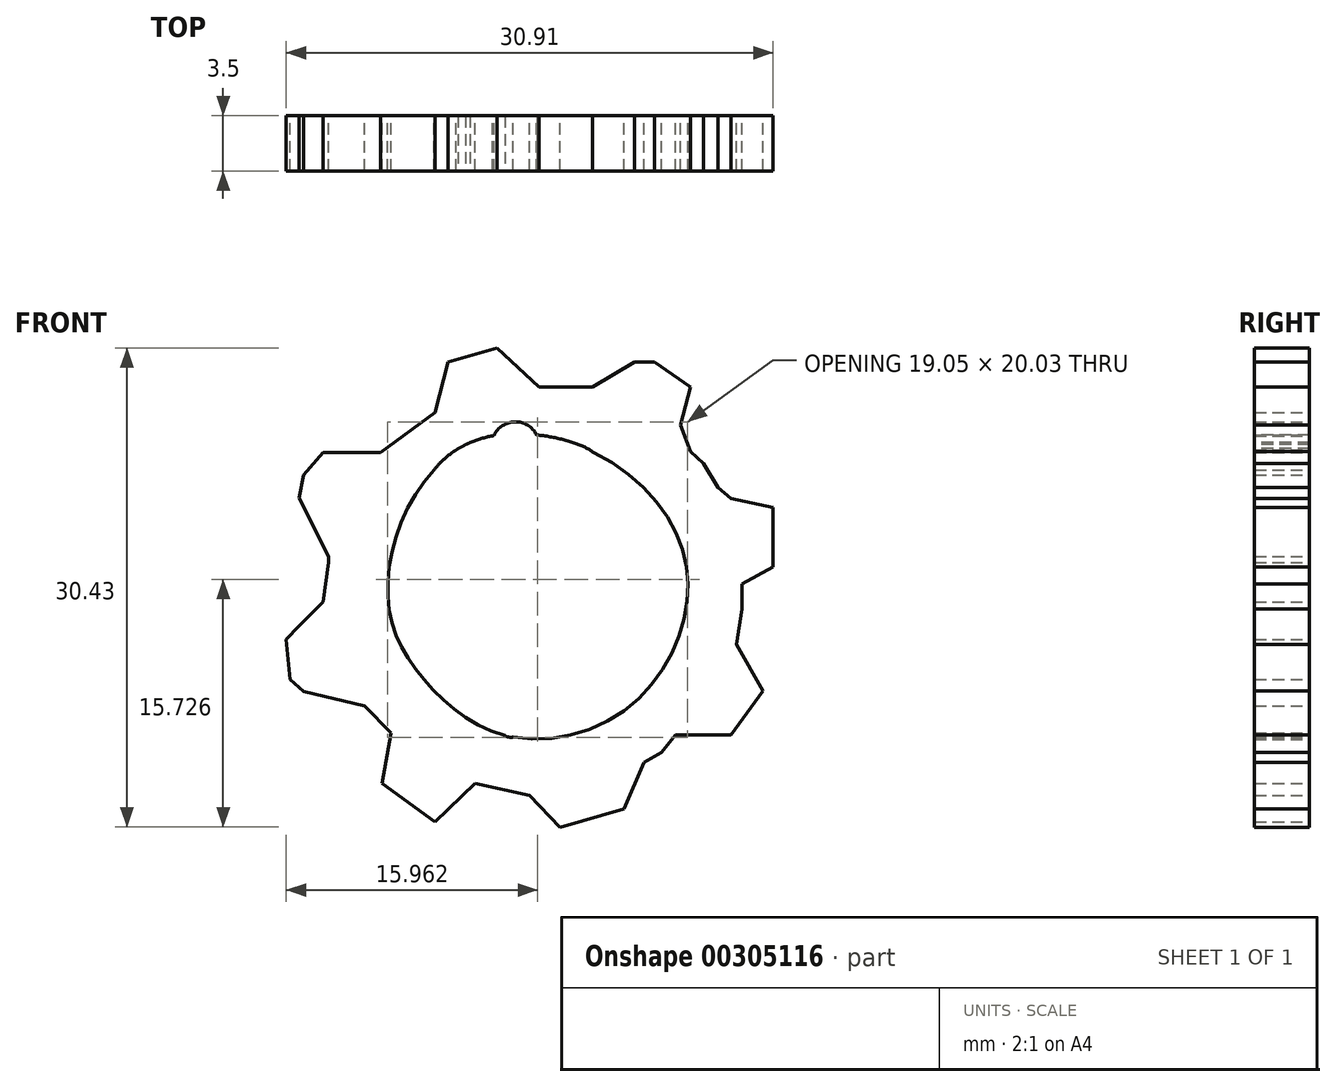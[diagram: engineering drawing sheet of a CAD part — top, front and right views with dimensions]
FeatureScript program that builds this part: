
annotation { "Feature Type Name" : "Feature", "Feature Type Description" : "" }
export const myFeature = defineFeature(function(context is Context, id is Id, definition is map)
    precondition{}
    {
        {
            var Q0;
            Q0=qCreatedBy(makeId("Front.planeOp"),FACE);
            var sketch = newSketch(context, id + "F0", { "sketchPlane" : qUnion([Q0])});
            skLineSegment(sketch, "E0", {"start": v(-29.85, 3.7) * mm, "end": v(-31.8, 5.73) * mm});
            skLineSegment(sketch, "E1", {"start": v(-31.8, 5.73) * mm, "end": v(-35.26, 6.5) * mm});
            skLineSegment(sketch, "E2", {"start": v(-35.26, 6.5) * mm, "end": v(-37.8, 4.04) * mm});
            skLineSegment(sketch, "E3", {"start": v(-37.8, 4.04) * mm, "end": v(-41.17, 6.5) * mm});
            skLineSegment(sketch, "E4", {"start": v(-41.17, 6.5) * mm, "end": v(-40.58, 9.7) * mm});
            skLineSegment(sketch, "E5", {"start": v(-40.58, 9.7) * mm, "end": v(-42.27, 11.4) * mm});
            skLineSegment(sketch, "E6", {"start": v(-42.27, 11.4) * mm, "end": v(-46.15, 12.32) * mm});
            skLineSegment(sketch, "E7", {"start": v(-46.15, 12.32) * mm, "end": v(-47, 13.08) * mm});
            skLineSegment(sketch, "E8", {"start": v(-47, 13.08) * mm, "end": v(-47.25, 15.63) * mm});
            skLineSegment(sketch, "E9", {"start": v(-47.25, 15.63) * mm, "end": v(-46.43, 16.48) * mm});
            skLineSegment(sketch, "E10", {"start": v(-46.43, 16.48) * mm, "end": v(-44.91, 18.03) * mm});
            skLineSegment(sketch, "E11", {"start": v(-44.91, 18.03) * mm, "end": v(-44.55, 20.5) * mm});
            skLineSegment(sketch, "E12", {"start": v(-44.55, 20.5) * mm, "end": v(-44.55, 20.9) * mm});
            skLineSegment(sketch, "E13", {"start": v(-44.55, 20.9) * mm, "end": v(-46.43, 24.6) * mm});
            skLineSegment(sketch, "E14", {"start": v(-46.43, 24.6) * mm, "end": v(-46.15, 26.07) * mm});
            skLineSegment(sketch, "E15", {"start": v(-46.15, 26.07) * mm, "end": v(-44.91, 27.5) * mm});
            skLineSegment(sketch, "E16", {"start": v(-44.91, 27.5) * mm, "end": v(-41.27, 27.5) * mm});
            skLineSegment(sketch, "E17", {"start": v(-41.27, 27.5) * mm, "end": v(-37.8, 30.03) * mm});
            skLineSegment(sketch, "E18", {"start": v(-37.8, 30.03) * mm, "end": v(-36.96, 33.26) * mm});
            skLineSegment(sketch, "E19", {"start": v(-36.96, 33.26) * mm, "end": v(-33.86, 34.14) * mm});
            skLineSegment(sketch, "E20", {"start": v(-33.86, 34.14) * mm, "end": v(-31.2, 31.68) * mm});
            skLineSegment(sketch, "E21", {"start": v(-31.2, 31.68) * mm, "end": v(-29.56, 31.68) * mm});
            skLineSegment(sketch, "E22", {"start": v(-29.56, 31.68) * mm, "end": v(-28.49, 31.68) * mm});
            skLineSegment(sketch, "E23", {"start": v(-28.49, 31.68) * mm, "end": v(-27.79, 31.68) * mm});
            skLineSegment(sketch, "E24", {"start": v(-27.79, 31.68) * mm, "end": v(-25.13, 33.26) * mm});
            skLineSegment(sketch, "E25", {"start": v(-25.13, 33.26) * mm, "end": v(-23.87, 33.26) * mm});
            skLineSegment(sketch, "E26", {"start": v(-23.87, 33.26) * mm, "end": v(-21.59, 31.68) * mm});
            skLineSegment(sketch, "E27", {"start": v(-21.59, 31.68) * mm, "end": v(-22.21, 29.25) * mm});
            skLineSegment(sketch, "E28", {"start": v(-22.21, 29.25) * mm, "end": v(-21.59, 27.56) * mm});
            skLineSegment(sketch, "E29", {"start": v(-21.59, 27.56) * mm, "end": v(-20.77, 26.8) * mm});
            skLineSegment(sketch, "E30", {"start": v(-20.77, 26.8) * mm, "end": v(-19.82, 25.29) * mm});
            skLineSegment(sketch, "E31", {"start": v(-19.82, 25.29) * mm, "end": v(-19, 24.59) * mm});
            skLineSegment(sketch, "E32", {"start": v(-19, 24.59) * mm, "end": v(-16.34, 24.02) * mm});
            skLineSegment(sketch, "E33", {"start": v(-16.34, 24.02) * mm, "end": v(-16.34, 20.22) * mm});
            skLineSegment(sketch, "E34", {"start": v(-16.34, 20.22) * mm, "end": v(-18.3, 19.15) * mm});
            skLineSegment(sketch, "E35", {"start": v(-18.3, 19.15) * mm, "end": v(-18.3, 17.57) * mm});
            skLineSegment(sketch, "E36", {"start": v(-18.3, 17.57) * mm, "end": v(-18.66, 15.32) * mm});
            skLineSegment(sketch, "E37", {"start": v(-18.66, 15.32) * mm, "end": v(-16.96, 12.37) * mm});
            skLineSegment(sketch, "E38", {"start": v(-16.96, 12.37) * mm, "end": v(-19, 9.56) * mm});
            skLineSegment(sketch, "E39", {"start": v(-19, 9.56) * mm, "end": v(-21.57, 9.56) * mm});
            skLineSegment(sketch, "E40", {"start": v(-21.57, 9.56) * mm, "end": v(-22.53, 9.56) * mm});
            skLineSegment(sketch, "E41", {"start": v(-22.53, 9.56) * mm, "end": v(-23.4, 8.44) * mm});
            skLineSegment(sketch, "E42", {"start": v(-23.4, 8.44) * mm, "end": v(-24.52, 7.8) * mm});
            skLineSegment(sketch, "E43", {"start": v(-24.52, 7.8) * mm, "end": v(-25.8, 4.85) * mm});
            skLineSegment(sketch, "E44", {"start": v(-25.8, 4.85) * mm, "end": v(-29.85, 3.7) * mm});
            skFitSpline(sketch, "E45", {"points": [v(-33.6, 20.27) * mm, v(-35.44, 20.7) * mm, v(-36.15, 19.61) * mm, v(-36.15, 19.08) * mm, v(-36.1, 18.52) * mm, v(-35.4, 18.19) * mm, v(-33.92, 18.62) * mm, v(-33.6, 20.27) * mm]});
            skFitSpline(sketch, "E46", {"points": [v(-30.94, 21.03) * mm, v(-28.94, 22.03) * mm, v(-27.9, 21.18) * mm, v(-28.14, 19.8) * mm, v(-30.8, 19.85) * mm, v(-30.95, 20.48) * mm, v(-30.94, 21.03) * mm]});
            skPoint(sketch, "E47.5.internal.snap0", {"position": v(-45.53, 26.79) * mm});
            skPoint(sketch, "E47.5.internal.snap1", {"position": v(-26.46, 32.47) * mm});
            skPoint(sketch, "E47.8.internal.snap0", {"position": v(-26.46, 32.47) * mm});
            skFitSpline(sketch, "E48", {"points": [v(-32.06, 16.68) * mm, v(-32.56, 17.1) * mm, v(-32.68, 18.19) * mm, v(-32.47, 19.08) * mm, v(-32.08, 18.52) * mm, v(-31.66, 17.17) * mm, v(-32.06, 16.68) * mm]});
            skFitSpline(sketch, "E49", {"points": [v(-31.48, 19.08) * mm, v(-31.57, 18.19) * mm, v(-31.21, 16.99) * mm, v(-30.47, 17.26) * mm, v(-30.94, 18.52) * mm, v(-31.48, 19.08) * mm]});
            skFitSpline(sketch, "E50", {"points": [v(-33.6, 12.98) * mm, v(-34.15, 13.04) * mm, v(-34.97, 14.36) * mm, v(-35.4, 15.22) * mm, v(-35, 15.22) * mm, v(-34.74, 14.9) * mm, v(-34.44, 14.94) * mm, v(-34.5, 14.48) * mm, v(-34.15, 13.82) * mm, v(-33.6, 13.52) * mm, v(-33.6, 12.98) * mm]});
            skFitSpline(sketch, "E51", {"points": [v(-32.91, 14.42) * mm, v(-32.56, 12.95) * mm, v(-32.69, 14.25) * mm, v(-32.87, 14.63) * mm, v(-32.91, 14.42) * mm]});
            skFitSpline(sketch, "E52", {"points": [v(-32.73, 12.91) * mm, v(-32.92, 13.58) * mm, v(-33.09, 13.63) * mm, v(-33.11, 13.75) * mm, v(-32.92, 13.72) * mm, v(-32.85, 13.55) * mm, v(-32.66, 12.96) * mm, v(-32.73, 12.91) * mm]});
            skFitSpline(sketch, "E53", {"points": [v(-32.22, 14.54) * mm, v(-32.15, 14.4) * mm, v(-32, 14.68) * mm, v(-32.03, 15.38) * mm, v(-31.84, 15.42) * mm, v(-31.6, 14.23) * mm, v(-31.43, 14.28) * mm, v(-31.43, 15.1) * mm, v(-30.95, 15.33) * mm, v(-30.79, 15.2) * mm, v(-30.83, 15.06) * mm, v(-30.7, 14.68) * mm, v(-30.6, 13.82) * mm, v(-30.25, 12.96) * mm, v(-30.4, 12.66) * mm, v(-30.9, 12.76) * mm, v(-31.13, 13.4) * mm, v(-31.35, 14.2) * mm, v(-31.38, 14.08) * mm, v(-31.6, 14.15) * mm, v(-31.9, 14.17) * mm, v(-31.88, 13.9) * mm, v(-32.2, 14.25) * mm, v(-32.22, 14.54) * mm]});
            skFitSpline(sketch, "E54", {"points": [v(-30.33, 15.06) * mm, v(-30.62, 15.32) * mm, v(-30.35, 15.5) * mm, v(-30.07, 15.42) * mm, v(-29.73, 15.47) * mm, v(-29.5, 15.47) * mm, v(-29.4, 14.76) * mm, v(-29.3, 14.4) * mm, v(-29.24, 14.4) * mm, v(-29.27, 15.4) * mm, v(-29.14, 15.5) * mm, v(-28.98, 15.2) * mm, v(-28.93, 15.06) * mm, v(-29.12, 14.94) * mm, v(-29.05, 14.54) * mm, v(-28.9, 14.56) * mm, v(-28.93, 14.4) * mm, v(-29.12, 14.4) * mm, v(-29.15, 14.28) * mm, v(-29.24, 14.28) * mm, v(-29.25, 14.34) * mm, v(-29.34, 14.35) * mm, v(-29.32, 13.85) * mm, v(-29.4, 13.84) * mm, v(-29.38, 13.55) * mm, v(-29.7, 13.54) * mm, v(-29.74, 13.84) * mm, v(-29.9, 14.06) * mm, v(-30, 14.28) * mm, v(-29.9, 14.4) * mm, v(-30.09, 14.54) * mm, v(-30.23, 14.94) * mm, v(-30.33, 15.06) * mm]});
            skFitSpline(sketch, "E55", {"points": [v(-30.43, 14.7) * mm, v(-30.36, 14.7) * mm, v(-30.32, 14.66) * mm, v(-30.24, 14.3) * mm, v(-29.83, 13.42) * mm, v(-29.89, 13.14) * mm, v(-30.1, 13.15) * mm, v(-30.13, 13.46) * mm, v(-30.29, 13.67) * mm, v(-30.32, 14.02) * mm, v(-30.3, 14.14) * mm, v(-30.42, 14.21) * mm, v(-30.5, 14.6) * mm, v(-30.43, 14.7) * mm]});
            skFitSpline(sketch, "E56", {"points": [v(-29.12, 13.55) * mm, v(-29.12, 14.06) * mm, v(-28.96, 14.02) * mm, v(-28.9, 13.6) * mm, v(-29.12, 13.55) * mm]});
            skFitSpline(sketch, "E57", {"points": [v(-28.76, 14.02) * mm, v(-28.82, 14.06) * mm, v(-28.79, 13.85) * mm, v(-28.73, 13.87) * mm, v(-28.76, 14.02) * mm]});
            skFitSpline(sketch, "E58", {"points": [v(-28.68, 15.5) * mm, v(-28.8, 15.5) * mm, v(-28.82, 15.18) * mm, v(-28.8, 14.94) * mm, v(-28.7, 14.54) * mm, v(-28.7, 14.4) * mm, v(-28.6, 14.52) * mm, v(-28.56, 14.74) * mm, v(-28.6, 14.94) * mm, v(-28.63, 15.06) * mm, v(-28.65, 15.1) * mm, v(-28.65, 15.3) * mm, v(-28.68, 15.5) * mm]});
            skFitSpline(sketch, "E59", {"points": [v(-28.19, 15.02) * mm, v(-28.32, 15.06) * mm, v(-28.3, 14.68) * mm, v(-28.17, 14.68) * mm, v(-28.08, 14.54) * mm, v(-27.98, 14.54) * mm, v(-28.03, 14.76) * mm, v(-28.12, 14.78) * mm, v(-28.17, 14.94) * mm, v(-28.19, 15.02) * mm]});
            skFitSpline(sketch, "E60", {"points": [v(-27.73, 14.28) * mm, v(-27.8, 14.48) * mm, v(-27.64, 14.46) * mm, v(-27.58, 14.28) * mm, v(-27.73, 14.28) * mm]});
            skFitSpline(sketch, "E61", {"points": [v(-27.48, 14.5) * mm, v(-27.25, 15.81) * mm, v(-27.32, 16.34) * mm, v(-27.36, 16.91) * mm, v(-28.05, 16.53) * mm, v(-28.06, 16) * mm, v(-27.87, 16.14) * mm, v(-27.68, 16.02) * mm, v(-27.57, 16.2) * mm, v(-27.37, 16.1) * mm, v(-27.42, 15.8) * mm, v(-27.54, 15.07) * mm, v(-27.75, 15.23) * mm, v(-27.9, 15.2) * mm, v(-27.73, 14.85) * mm, v(-27.48, 14.5) * mm]});
            skFitSpline(sketch, "E62", {"points": [v(-26.75, 16.52) * mm, v(-27, 16.53) * mm, v(-26.94, 16.16) * mm, v(-26.9, 15.94) * mm, v(-27.05, 15.8) * mm, v(-27.12, 15.52) * mm, v(-27.17, 15.37) * mm, v(-27.24, 15.1) * mm, v(-27.17, 14.76) * mm, v(-27.06, 14.55) * mm, v(-27, 14.84) * mm, v(-26.9, 15.26) * mm, v(-26.84, 15.53) * mm, v(-26.82, 15.8) * mm, v(-26.75, 16.16) * mm, v(-26.83, 16.29) * mm, v(-26.75, 16.52) * mm]});
            skPoint(sketch, "E63.2.internal.snap0", {"position": v(-35.41, 33.7) * mm});
            skFitSpline(sketch, "E64.trimOffspring", {"points": [v(-33.37, 9.53) * mm, v(-38.43, 13) * mm, v(-40.74, 17.7) * mm, v(-39.3, 24.42) * mm, v(-34.15, 28.56) * mm, v(-26.46, 26.79) * mm, v(-22.16, 21.55) * mm, v(-22.32, 15.8) * mm, v(-26.46, 10.66) * mm, v(-33.37, 9.53) * mm]});
            skFitSpline(sketch, "E65.trimOffspring", {"points": [v(-37.87, 26.38) * mm, v(-36.47, 27.66) * mm, v(-36.33, 27.74) * mm, v(-35.85, 28) * mm, v(-35.56, 28.13) * mm, v(-34.15, 28.56) * mm, v(-31.33, 28.62) * mm, v(-27.75, 27.5) * mm, v(-26.97, 26.52) * mm, v(-26.46, 26.07) * mm, v(-26.46, 23.07) * mm, v(-27.14, 21.9) * mm, v(-27.14, 19.95) * mm, v(-25.83, 18.95) * mm, v(-26, 17.92) * mm, v(-26.46, 17.4) * mm, v(-26.75, 14.55) * mm, v(-27.13, 11.93) * mm, v(-29.16, 10.63) * mm, v(-33.37, 9.53) * mm, v(-33.37, 10.53) * mm, v(-34.3, 11.06) * mm, v(-35.4, 13.27) * mm, v(-36.87, 14.35) * mm], "startDerivative": vector(38.58, 35.58) * mm, "endDerivative": vector(-36.08, 16.17) * mm});
            skFitSpline(sketch, "E66.trimOffspring", {"points": [v(-33.37, 9.53) * mm, v(-33.37, 10.53) * mm, v(-34.3, 11.06) * mm, v(-35.4, 13.27) * mm, v(-36.87, 14.35) * mm, v(-38.72, 17.45) * mm, v(-38.54, 19.61) * mm, v(-39.55, 21.34) * mm, v(-38.6, 24.74) * mm, v(-37.87, 26.38) * mm, v(-34.15, 28.56) * mm, v(-27.75, 27.5) * mm, v(-26.97, 26.52) * mm, v(-26.46, 26.07) * mm, v(-26.46, 23.07) * mm, v(-27.14, 21.9) * mm, v(-27.14, 19.95) * mm, v(-25.83, 18.95) * mm, v(-26, 17.92) * mm, v(-26.46, 17.4) * mm, v(-26.75, 14.66) * mm, v(-27.13, 11.93) * mm, v(-29.16, 10.63) * mm, v(-33.37, 9.53) * mm]});
            skPoint(sketch, "E67.20.internal.orphan", {"position": v(-26.75, 14.76) * mm});
            skPoint(sketch, "E68.13.internal.orphan", {"position": v(-25.83, 19.08) * mm});
            skLineSegment(sketch, "E69.trimOffspring", {"start": v(-32.86, 9.42) * mm, "end": v(-32.86, 9.42) * mm});
            skSolve(sketch);
        }
        {
            var Q0;
            Q0=qCreatedBy(makeId("Front.planeOp"),FACE);
            var sketch = newSketch(context, id + "F1", { "sketchPlane" : qUnion([Q0])});
            skCircle(sketch, "E70", {"center": v(-32.7, 27.95) * mm, "radius": 1.5 * mm});
            skSolve(sketch);
        }
        {
            var Q0;
            Q0=makeQuery(id+"F0.imprint","IMPRINT",FACE,{"disambiguationData":[TD([[makeQuery(id+"F0.imprint","IMPRINT",EDGE,{"derivedFrom":sQuery(id+"F0.wireOp",EDGE,"E0")}),-1.0]])]});
            extrude(context, id + "F2", {"entities" : qUnion([Q0]), "depth" : 3.5 * mm});
        }
        {
            var Q0;
            Q0=makeQuery(id+"F1.imprint","IMPRINT",FACE,{"disambiguationData":[TD([[makeQuery(id+"F1.imprint","IMPRINT",EDGE,{"derivedFrom":sQuery(id+"F1.wireOp",EDGE,"E70")}),1.0]])]});
            var Q1;
            Q1=sQuery(id+"F1.wireOp",EDGE,"E70");
            extrude(context, id + "F3", {"entities" : qUnion([Q0]), "operationType" : NewBodyOperationType.REMOVE, "surfaceEntities" : qUnion([Q1]), "depth" : 25 * mm});
        }
    });
